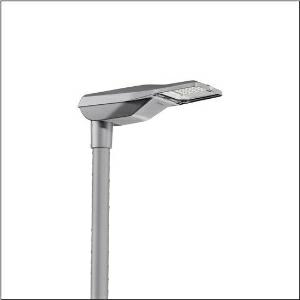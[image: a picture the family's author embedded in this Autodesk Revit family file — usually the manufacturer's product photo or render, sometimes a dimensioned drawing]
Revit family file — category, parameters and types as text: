
# Revit family: streetlight_sl_21_iq_micro___st0_8a_5xe1c41d08cb_e31f
name_source: partatom
category: Lighting Fixtures
units: mm (PartAtom-declared; Revit-internal decimal feet)

## family parameters
Cut with Voids When Loaded = No
Host = Face
Light Source = No
Part Type = Normal
Room Calculation Point = No
Round Connector Dimension = Use Diameter
Shared = No

## types (1)
- --- (1 x LED, 2980 lm, 19.4 W, 4000K)
    Apparent Load = 19 VA
    CIE Flux Codes = 38 75 97 100 100
    Color Rendering = 70
    Color Temperature = 4000K
    Default Elevation = 1800 mm
    Description = Streetlight SL 21 iQ micro, mast luminaire, primary light control with lens, of PMMA, primary optical cover: cover, of toughened safety glass, transparent, light distribution: ST0.8a, light emission: direct distribution, primary light characteristic: asymmetric, installation type: post-top, side-entry, LED, High Power LED, rated luminous flux: 2.980lm, luminous efficacy: 154lm/W, light colour: 740, colour temperature: 4000K, control gear: iQ-Comfort, control: Auto-Match, Temp-Guard, Lumen-Switch, Night-Set, Smart-Wire, Light-Fading, Desk-Remote (wireless, voltage-free reading and setting of iQ features in the workshop via application-optimized NFC function/RFID function), optimised constant luminous flux control (CLO 2.0), pre-setting: linear dimming characteristic, mains connection: 220..240V, AC, 50/60Hz, start of lifetime: 19W, end of service life: 20W, reduction: 10W, luminaire housing, of diecast aluminium, powder-coated, Siteco® metallic grey (DB 702S), corrosivity category C5 mid according to DIN EN ISO 12944, please order mast flange separately, inclination adjustable: 0°, 5°, 10°, 15°, sealing non-destructively replaceable, multi-level sealing system, length: 528mm, width: 235mm, height: 110mm, mast flange for spigot size: 42mm (side-entry): 5XC10008XM4, 60/48mm (side-entry/post-top): 5XC10108XM2, 76/60mm (side-entry/post-top): 5XC10108XM1, protection rating (complete): IP66, insulation class (complete): insulation class II (safety insulation), certification: CE, ENEC, ENEC+, VDE, impact resistance: IK10, permissible operating ambient temperature for outdoor applications: -40..+50°C, standard-compliant lighting for roads and squares, packaging unit: 1 piece

Light Distribution: ST0.8a
    Height = 110 mm
    Lamp = 1 x LED
    Lamp Light Flux = 2980 lm
    Lamp Power = 19.4 W
    Lamp count = 1
    Length = 528 mm
    Luminous efficacy = 154 lm/W
    Manufacturer = Siteco
    ModVariant = No
    Model = 5XE1C41D08CB
    Number of Poles = 1
    OnlyDefault = Yes
    Power Factor = 1
    Product Name = Streetlight SL 21 iQ micro | ST0.8a
    Product group = mast luminaire | pylon top
    ProductGroupID = 6100
    Protection Class = Protection class II
    Protection Degree = IP 66
    RLX_Detail_Level = 1
    RLX_Emergency_Light_Flux = 0 lm
    RLX_Emergency_Type = 0
    RLX_Emergency_Type_DB = No
    RlxData = <blob elided: 98493 chars, md5=28a2f575>
    Socket = socket
    Standby Power = 0 W
    System Light Flux = 2980 lm
    System Power = 19 W
    Type Comments = factory setting: luminous flux: 100 % | dim-lin: 254 | 387 mA
    Type Image = l_1006881.jpg
    URL = http://relux.com
    VarID = @adj_159871
    Voltage = 0 V
    Weight = 0.00 kg
    Width = 235 mm

## geometry (parser evidence)
native form markers: Blend x4, Sweep x9
no freeform markers — native parametric forms only
